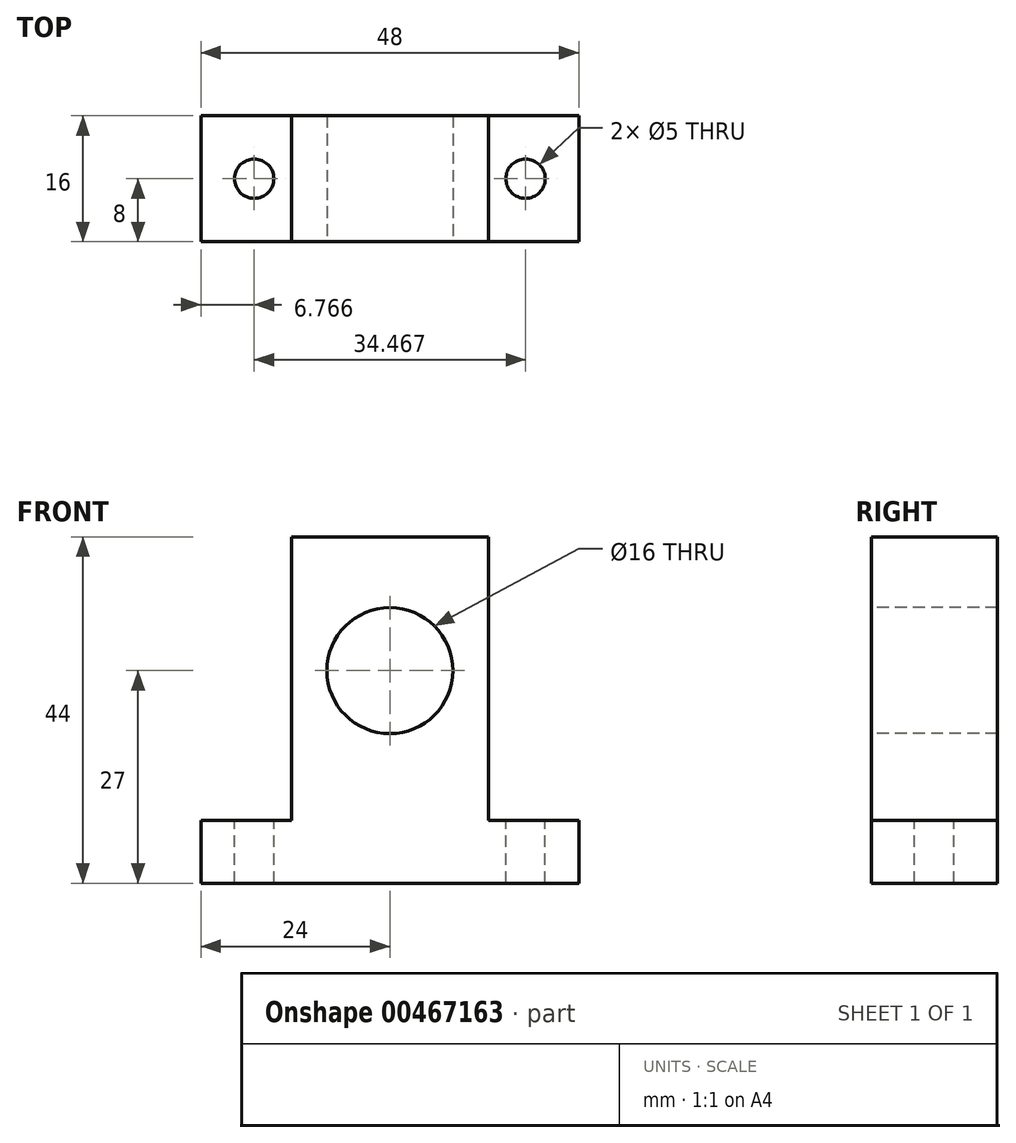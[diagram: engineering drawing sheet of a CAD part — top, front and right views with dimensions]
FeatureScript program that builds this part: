
annotation { "Feature Type Name" : "Feature", "Feature Type Description" : "" }
export const myFeature = defineFeature(function(context is Context, id is Id, definition is map)
    precondition{}
    {
        {
            var Q0;
            Q0=qCreatedBy(makeId("Front.planeOp"),FACE);
            var sketch = newSketch(context, id + "F0", { "sketchPlane" : qUnion([Q0])});
            skLineSegment(sketch, "E0", {"start": v(0, 0) * mm, "end": v(24, 0) * mm});
            skLineSegment(sketch, "E1", {"start": v(24, 0) * mm, "end": v(24, 8) * mm});
            skLineSegment(sketch, "E2", {"start": v(24, 8) * mm, "end": v(12.5, 8) * mm});
            skLineSegment(sketch, "E3", {"start": v(12.5, 8) * mm, "end": v(12.5, 44) * mm});
            skLineSegment(sketch, "E4", {"start": v(12.5, 44) * mm, "end": v(0, 44) * mm});
            skLineSegment(sketch, "E5.MirrorCS", {"start": v(-12.5, 44) * mm, "end": v(0, 44) * mm});
            skLineSegment(sketch, "E6.MirrorCS", {"start": v(-12.5, 8) * mm, "end": v(-12.5, 44) * mm});
            skLineSegment(sketch, "E7.MirrorCS", {"start": v(-24, 8) * mm, "end": v(-12.5, 8) * mm});
            skLineSegment(sketch, "E8.MirrorCS", {"start": v(-24, 0) * mm, "end": v(-24, 8) * mm});
            skLineSegment(sketch, "E9.MirrorCS", {"start": v(0, 0) * mm, "end": v(-24, 0) * mm});
            skLineSegment(sketch, "E10", {"start": v(0, 0) * mm, "end": v(0, 27) * mm, "construction": true});
            skCircle(sketch, "E11", {"center": v(0, 27) * mm, "radius": 8 * mm});
            skSolve(sketch);
        }
        {
            var Q0;
            Q0=makeQuery(id+"F0.imprint","IMPRINT",FACE,{"disambiguationData":[TD([[makeQuery(id+"F0.imprint","IMPRINT",EDGE,{"derivedFrom":sQuery(id+"F0.wireOp",EDGE,"E0")}),1.0]])]});
            extrude(context, id + "F1", {"entities" : qUnion([Q0]), "oppositeDirection" : true, "depth" : 8 * mm, "hasSecondDirection" : true, "secondDirectionOppositeDirection" : false, "secondDirectionDepth" : 8 * mm});
        }
        {
            var Q0;
            Q0=makeQuery(id+"F1.opExtrude","SWEPT_FACE",FACE,{"disambiguationData":[OSD([sQuery(id+"F0.wireOp",EDGE,"E2")])]});
            var sketch = newSketch(context, id + "F2", { "sketchPlane" : qUnion([Q0])});
            skLineSegment(sketch, "E12", {"start": v(0, 0) * mm, "end": v(17.23, -8) * mm, "construction": true});
            skLineSegment(sketch, "E13", {"start": v(17.23, -8) * mm, "end": v(17.23, 0) * mm, "construction": true});
            skLineSegment(sketch, "E14.MirrorCS", {"start": v(0, 0) * mm, "end": v(-17.23, -8) * mm, "construction": true});
            skLineSegment(sketch, "E15.MirrorCS", {"start": v(-17.23, -8) * mm, "end": v(-17.23, 0) * mm, "construction": true});
            skSolve(sketch);
        }
        {
            var Q0;
            Q0=sQuery(id+"F2.wireOp",VERTEX,"E15.MirrorCS.end");
            var Q1;
            Q1=sQuery(id+"F2.wireOp",VERTEX,"E13.end");
            var Q2;
            Q2=makeQuery(id+"F1.opExtrude","SWEPT_BODY",BODY,{"disambiguationData":[OSD([sQuery(id+"F0.wireOp",EDGE,"E0"),sQuery(id+"F0.wireOp",EDGE,"E1"),sQuery(id+"F0.wireOp",EDGE,"E2"),sQuery(id+"F0.wireOp",EDGE,"E3"),sQuery(id+"F0.wireOp",EDGE,"E4"),sQuery(id+"F0.wireOp",EDGE,"E5.MirrorCS"),sQuery(id+"F0.wireOp",EDGE,"E6.MirrorCS"),sQuery(id+"F0.wireOp",EDGE,"E7.MirrorCS"),sQuery(id+"F0.wireOp",EDGE,"E8.MirrorCS"),sQuery(id+"F0.wireOp",EDGE,"E9.MirrorCS"),sQuery(id+"F0.wireOp",EDGE,"E11")])]});
            hole(context, id + "F3", {"style" : HoleStyle.SIMPLE, "endStyle" : HoleEndStyle.THROUGH, "holeDiameter" : 5 * mm, "isTappedThrough" : true, "tappedDepth" : 12 * mm, "tapClearance" : 3, "locations" : qUnion([Q0, Q1]), "scope" : qUnion([Q2])});
        }
    });
